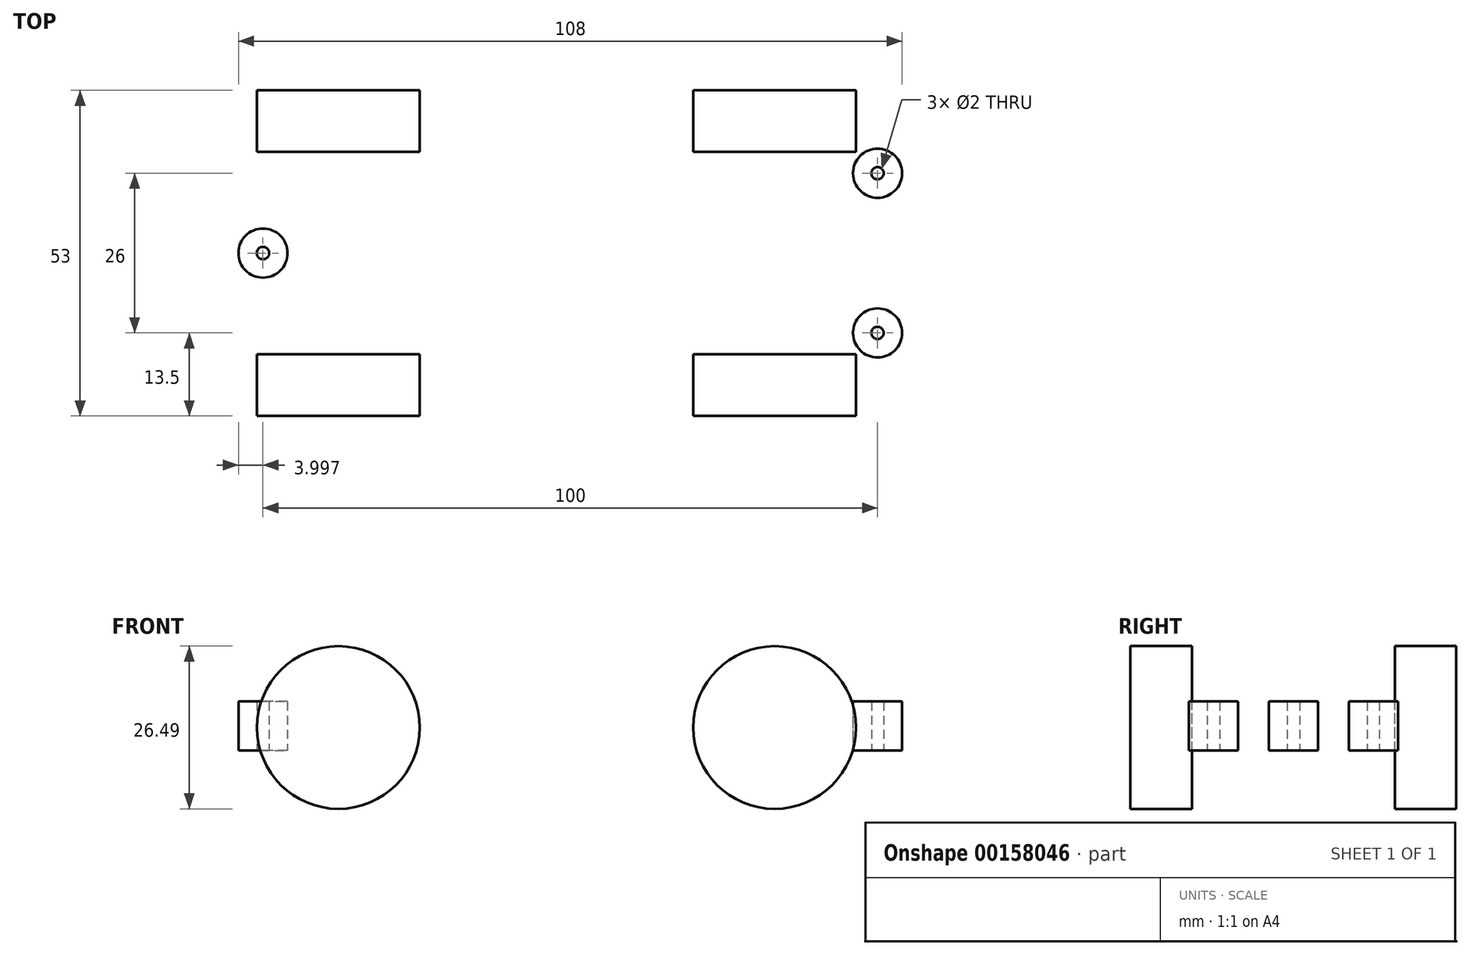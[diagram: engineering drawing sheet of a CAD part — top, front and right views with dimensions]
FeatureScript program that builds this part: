
annotation { "Feature Type Name" : "Feature", "Feature Type Description" : "" }
export const myFeature = defineFeature(function(context is Context, id is Id, definition is map)
    precondition{}
    {
        {
            var Q0;
            Q0=qCreatedBy(makeId("Top.planeOp"),FACE);
            var sketch = newSketch(context, id + "F0", { "sketchPlane" : qUnion([Q0])});
            skLineSegment(sketch, "E0", {"start": v(-78.5, 0) * mm, "end": v(21.5, 0) * mm, "construction": true});
            skLineSegment(sketch, "E1", {"start": v(21.5, 0) * mm, "end": v(21.5, 13) * mm, "construction": true});
            skLineSegment(sketch, "E2", {"start": v(21.5, 0) * mm, "end": v(21.5, -13) * mm, "construction": true});
            skCircle(sketch, "E3", {"center": v(-78.5, 0) * mm, "radius": 1 * mm});
            skCircle(sketch, "E4", {"center": v(21.5, 13) * mm, "radius": 1 * mm});
            skCircle(sketch, "E5", {"center": v(21.5, -13) * mm, "radius": 1 * mm});
            skCircle(sketch, "E6", {"center": v(-78.5, 0) * mm, "radius": 4 * mm});
            skCircle(sketch, "E7", {"center": v(21.5, 13) * mm, "radius": 4 * mm});
            skCircle(sketch, "E8", {"center": v(21.5, -13) * mm, "radius": 4 * mm});
            skLineSegment(sketch, "E9.bottom", {"start": v(-83, 26.5) * mm, "end": v(27.5, 26.5) * mm, "construction": true});
            skLineSegment(sketch, "E9.top", {"start": v(-83, -26.5) * mm, "end": v(27.5, -26.5) * mm, "construction": true});
            skLineSegment(sketch, "E9.left", {"start": v(-83, 26.5) * mm, "end": v(-83, -26.5) * mm, "construction": true});
            skLineSegment(sketch, "E9.right", {"start": v(27.5, 26.5) * mm, "end": v(27.5, -26.5) * mm, "construction": true});
            skLineSegment(sketch, "E10", {"start": v(-66.23, 26.5) * mm, "end": v(-66.23, -26.5) * mm, "construction": true});
            skLineSegment(sketch, "E11", {"start": v(4.75, 26.5) * mm, "end": v(4.75, -26.5) * mm, "construction": true});
            skSolve(sketch);
        }
        {
            var Q0;
            Q0=makeQuery(id+"F0.imprint","IMPRINT",FACE,{"disambiguationData":[TD([[makeQuery(id+"F0.imprint","IMPRINT",EDGE,{"derivedFrom":sQuery(id+"F0.wireOp",EDGE,"E3")}),-1.0]])]});
            var Q1;
            Q1=makeQuery(id+"F0.imprint","IMPRINT",FACE,{"disambiguationData":[TD([[makeQuery(id+"F0.imprint","IMPRINT",EDGE,{"derivedFrom":sQuery(id+"F0.wireOp",EDGE,"E4")}),-1.0]])]});
            var Q2;
            Q2=makeQuery(id+"F0.imprint","IMPRINT",FACE,{"disambiguationData":[TD([[makeQuery(id+"F0.imprint","IMPRINT",EDGE,{"derivedFrom":sQuery(id+"F0.wireOp",EDGE,"E5")}),-1.0]])]});
            var Q3;
            Q3=sQuery(id+"F0.wireOp",EDGE,"E6");
            var Q4;
            Q4=sQuery(id+"F0.wireOp",EDGE,"E7");
            var Q5;
            Q5=sQuery(id+"F0.wireOp",EDGE,"E8");
            var Q6;
            Q6=sQuery(id+"F0.wireOp",EDGE,"E5");
            var Q7;
            Q7=sQuery(id+"F0.wireOp",EDGE,"E3");
            var Q8;
            Q8=sQuery(id+"F0.wireOp",EDGE,"E4");
            extrude(context, id + "F1", {"entities" : qUnion([Q0, Q1, Q2]), "surfaceEntities" : qUnion([Q3, Q4, Q5, Q6, Q7, Q8]), "depth" : 8 * mm});
        }
        {
            var Q0;
            Q0=qCreatedBy(makeId("Front.planeOp"),FACE);
            cPlane(context, id + "F2", {"entities" : qUnion([Q0]), "cplaneType" : CPlaneType.OFFSET, "offset" : 26.5 * mm, "width" : 150 * mm, "height" : 150 * mm});
        }
        {
            var Q0;
            Q0=qCreatedBy(id+"F2.planeOp",FACE);
            var sketch = newSketch(context, id + "F3", { "sketchPlane" : qUnion([Q0])});
            skLineSegment(sketch, "E12", {"start": v(-82.64, 3.77) * mm, "end": v(54.33, 3.77) * mm, "construction": true});
            skCircle(sketch, "E13", {"center": v(-66.23, 3.77) * mm, "radius": 13.24 * mm});
            skCircle(sketch, "E14", {"center": v(4.75, 3.77) * mm, "radius": 13.24 * mm});
            skLineSegment(sketch, "E15", {"start": v(-66.23, 0) * mm, "end": v(-66.23, 9.16) * mm, "construction": true});
            skLineSegment(sketch, "E16", {"start": v(4.75, 0) * mm, "end": v(4.75, 8.53) * mm, "construction": true});
            skSolve(sketch);
        }
        {
            var Q0;
            Q0=qSketchRegion(id+"F3",true);
            extrude(context, id + "F4", {"entities" : qUnion([Q0]), "oppositeDirection" : true, "depth" : 10 * mm});
        }
        {
            var Q0;
            Q0=makeQuery(id+"F4.opExtrude","SWEPT_BODY",BODY,{"disambiguationData":[OSD([sQuery(id+"F3.wireOp",EDGE,"E14")])]});
            var Q1;
            Q1=makeQuery(id+"F4.opExtrude","SWEPT_BODY",BODY,{"disambiguationData":[OSD([sQuery(id+"F3.wireOp",EDGE,"E13")])]});
            var Q2;
            Q2=qCreatedBy(makeId("Front.planeOp"),FACE);
            mirror(context, id + "F5", {"entities" : qUnion([Q0, Q1]), "mirrorPlane" : qUnion([Q2])});
        }
    });
